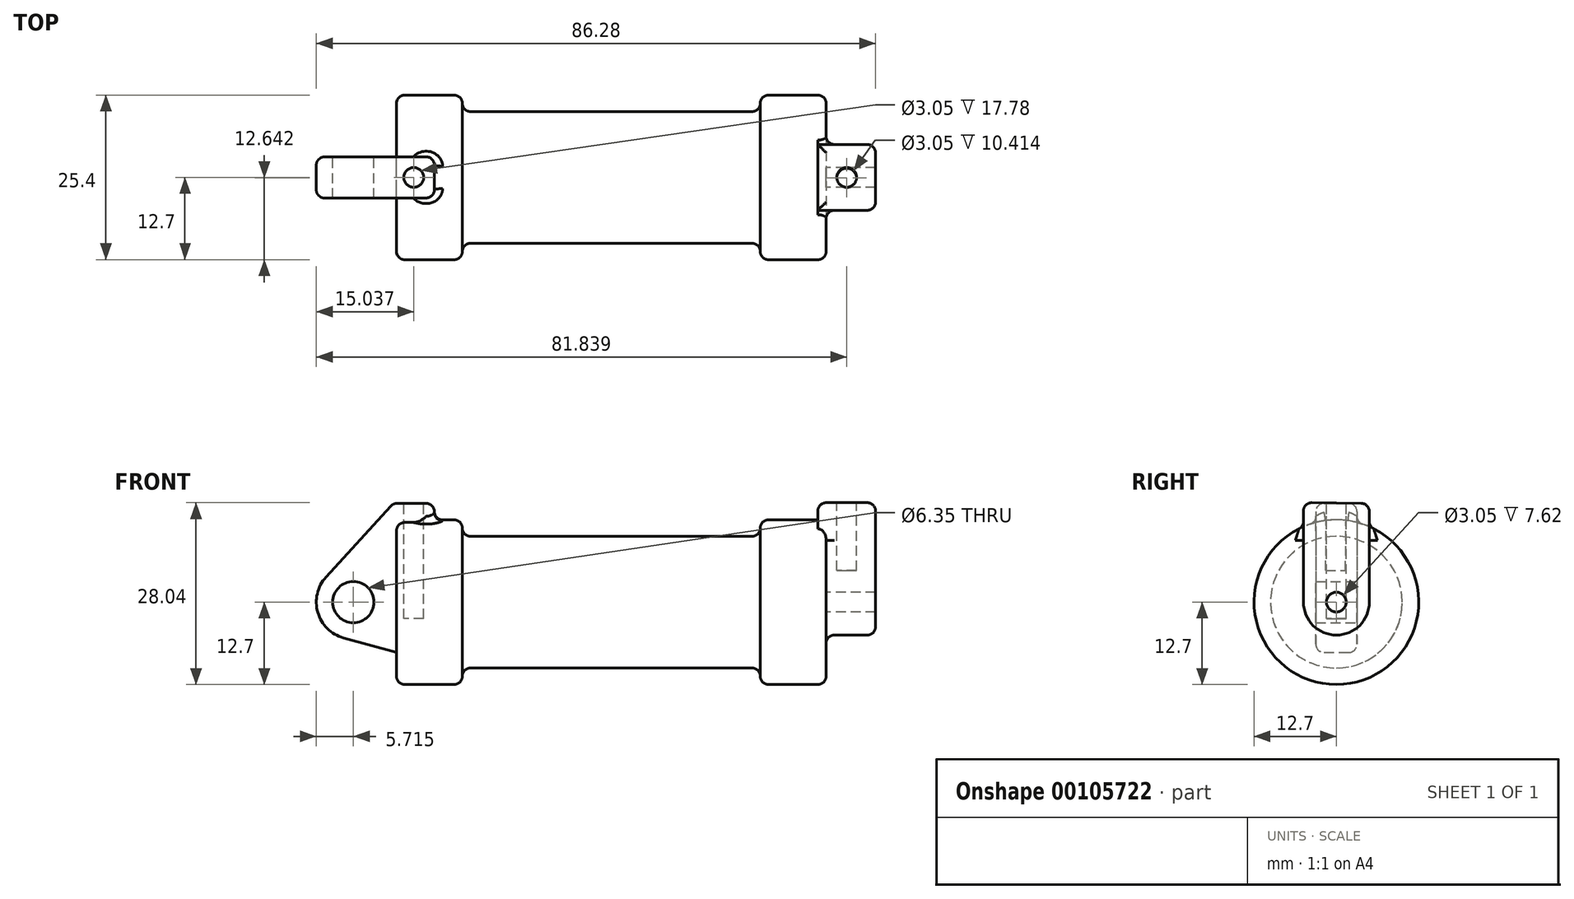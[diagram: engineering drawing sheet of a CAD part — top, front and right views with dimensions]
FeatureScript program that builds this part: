
annotation { "Feature Type Name" : "Feature", "Feature Type Description" : "" }
export const myFeature = defineFeature(function(context is Context, id is Id, definition is map)
    precondition{}
    {
        {
            var Q0;
            Q0=qCreatedBy(makeId("Front.planeOp"),FACE);
            var sketch = newSketch(context, id + "F0", { "sketchPlane" : qUnion([Q0])});
            skLineSegment(sketch, "E0", {"start": v(0, 0) * mm, "end": v(0, 12.7) * mm});
            skLineSegment(sketch, "E1", {"start": v(0, 12.7) * mm, "end": v(10.16, 12.7) * mm});
            skLineSegment(sketch, "E2", {"start": v(10.16, 12.7) * mm, "end": v(10.16, 10.16) * mm});
            skLineSegment(sketch, "E3", {"start": v(10.16, 10.16) * mm, "end": v(56.13, 10.16) * mm});
            skLineSegment(sketch, "E4", {"start": v(56.13, 10.16) * mm, "end": v(56.13, 12.7) * mm});
            skLineSegment(sketch, "E5", {"start": v(56.13, 12.7) * mm, "end": v(66.3, 12.7) * mm});
            skLineSegment(sketch, "E6", {"start": v(66.3, 12.7) * mm, "end": v(66.3, 0) * mm});
            skLineSegment(sketch, "E7", {"start": v(66.3, 0) * mm, "end": v(0, 0) * mm});
            skLineSegment(sketch, "E8", {"start": v(5.84, 15.24) * mm, "end": v(-0.5, 15.24) * mm});
            skLineSegment(sketch, "E9", {"start": v(-0.5, 15.24) * mm, "end": v(-10.88, 3.85) * mm});
            skLineSegment(sketch, "E10", {"start": v(0, 0) * mm, "end": v(-6.65, 0) * mm});
            skCircle(sketch, "E11", {"center": v(-6.65, 0) * mm, "radius": 5.72 * mm});
            skCircle(sketch, "E12", {"center": v(-6.65, 0) * mm, "radius": 3.18 * mm});
            skLineSegment(sketch, "E13", {"start": v(5.84, 15.24) * mm, "end": v(5.84, -9.4) * mm});
            skLineSegment(sketch, "E14", {"start": v(5.84, -9.4) * mm, "end": v(-8.18, -5.5) * mm});
            skSolve(sketch);
        }
        {
            var Q0;
            {var subQ0=sQuery(id+"F0.wireOp",EDGE,"E2");Q0=makeQuery(id+"F0.imprint","IMPRINT",FACE,{"disambiguationData":[TD([[makeQuery(id+"F0.imprint","IMPRINT",EDGE,{"derivedFrom":subQ0}),-1.0]])]});}
            var Q1;
            {var subQ0=sQuery(id+"F0.wireOp",EDGE,"E0");Q1=makeQuery(id+"F0.imprint","IMPRINT",FACE,{"disambiguationData":[TD([[makeQuery(id+"F0.imprint","IMPRINT",EDGE,{"derivedFrom":subQ0}),-1.0]])]});}
            var Q2;
            Q2=sQuery(id+"F0.wireOp",EDGE,"E7");
            revolve(context, id + "F1", {"entities" : qUnion([Q0, Q1]), "axis" : qUnion([Q2]), "revolveType" : RevolveType.FULL});
        }
        {
            var Q0;
            {var subQ3=sQuery(id+"F0.wireOp",EDGE,"E0");Q0=makeQuery(id+"F0.imprint","IMPRINT",FACE,{"disambiguationData":[TD([[makeQuery(id+"F0.imprint","IMPRINT",EDGE,{"derivedFrom":subQ3}),1.0]])]});}
            var Q1;
            {var subQ0=sQuery(id+"F0.wireOp",EDGE,"E14");Q1=makeQuery(id+"F0.imprint","IMPRINT",FACE,{"disambiguationData":[TD([[makeQuery(id+"F0.imprint","IMPRINT",EDGE,{"derivedFrom":subQ0}),-1.0]])]});}
            var Q2;
            {var subQ4=sQuery(id+"F0.wireOp",EDGE,"E12");Q2=makeQuery(id+"F0.imprint","IMPRINT",FACE,{"disambiguationData":[TD([[makeQuery(id+"F0.imprint","IMPRINT",EDGE,{"derivedFrom":subQ4}),-1.0]])]});}
            var Q3;
            {var subQ0=sQuery(id+"F0.wireOp",EDGE,"E0");Q3=makeQuery(id+"F0.imprint","IMPRINT",FACE,{"disambiguationData":[TD([[makeQuery(id+"F0.imprint","IMPRINT",EDGE,{"derivedFrom":subQ0}),-1.0]])]});}
            var Q4;
            Q4 = qSketchRegion(id + "F3", true);
            extrude(context, id + "F2", {"entities" : qUnion([Q0, Q1, Q2, Q3, Q4]), "operationType" : NewBodyOperationType.ADD, "endBound" : BoundingType.SYMMETRIC, "depth" : 6.35 * mm});
        }
        {
            var Q0;
            Q0=makeQuery(id+"F1.opRevolve","SWEPT_FACE",FACE,{"disambiguationData":[OSD([sQuery(id+"F0.wireOp",EDGE,"E6")])]});
            var sketch = newSketch(context, id + "F3", { "sketchPlane" : qUnion([Q0])});
            skCircle(sketch, "E15", {"center": v(0, 0) * mm, "radius": 1.52 * mm});
            skCircle(sketch, "E16", {"center": v(0, 0) * mm, "radius": 5.08 * mm});
            skLineSegment(sketch, "E17", {"start": v(-5.08, 0) * mm, "end": v(-5.08, 15.35) * mm});
            skLineSegment(sketch, "E18", {"start": v(5.08, 0) * mm, "end": v(5.08, 15.24) * mm});
            skLineSegment(sketch, "E19", {"start": v(-5.08, 15.35) * mm, "end": v(5.08, 15.24) * mm});
            skSolve(sketch);
        }
        {
            var Q0;
            Q0=makeQuery(id+"F3.imprint","IMPRINT",FACE,{"disambiguationData":[TD([[makeQuery(id+"F3.imprint","IMPRINT",EDGE,{"derivedFrom":sQuery(id+"F3.wireOp",EDGE,"E15")}),-1.0]])]});
            var Q1;
            {var subQ0=sQuery(id+"F3.wireOp",EDGE,"E17");var subQ1=sQuery(id+"F3.wireOp",EDGE,"E16");var subQ2=makeQuery(id+"F3.imprint","INTERSECT",VERTEX,{"derivedFrom":[subQ1,subQ0]});Q1=makeQuery(id+"F3.imprint","IMPRINT",FACE,{"disambiguationData":[TD([[makeQuery(id+"F3.imprint","IMPRINT",EDGE,{"disambiguationData":[TD([[subQ2,1.0]])],"derivedFrom":subQ1}),-1.0]])]});}
            var Q2;
            {var subQ0=sQuery(id+"F3.wireOp",EDGE,"E19");Q2=makeQuery(id+"F3.imprint","IMPRINT",FACE,{"disambiguationData":[TD([[makeQuery(id+"F3.imprint","IMPRINT",EDGE,{"derivedFrom":subQ0}),-1.0]])]});}
            extrude(context, id + "F4", {"entities" : qUnion([Q0, Q1, Q2]), "operationType" : NewBodyOperationType.ADD, "depth" : 7.62 * mm, "hasSecondDirection" : true, "secondDirectionOppositeDirection" : true, "secondDirectionDepth" : 1.27 * mm});
        }
        {
            var Q0;
            Q0=makeQuery(id+"F2.opExtrude","SWEPT_FACE",FACE,{"disambiguationData":[OSD([sQuery(id+"F0.wireOp",EDGE,"E8")])]});
            var sketch = newSketch(context, id + "F5", { "sketchPlane" : qUnion([Q0])});
            skPoint(sketch, "E20.centerSnap0", {"position": v(-0.5, 0) * mm});
            skLineSegment(sketch, "E21", {"start": v(-0.5, 0) * mm, "end": v(5.84, 0) * mm, "construction": true});
            skLineSegment(sketch, "E22", {"start": v(2.67, 3.18) * mm, "end": v(2.67, -3.18) * mm, "construction": true});
            skCircle(sketch, "E23", {"center": v(2.67, 0) * mm, "radius": 1.52 * mm});
            skSolve(sketch);
        }
        {
            var Q0;
            Q0=makeQuery(id+"F4.opExtrude","SWEPT_FACE",FACE,{"disambiguationData":[OSD([sQuery(id+"F3.wireOp",EDGE,"E19")])]});
            var sketch = newSketch(context, id + "F6", { "sketchPlane" : qUnion([Q0])});
            skLineSegment(sketch, "E24", {"start": v(69.47, 4.9) * mm, "end": v(69.47, -5.25) * mm, "construction": true});
            skLineSegment(sketch, "E25", {"start": v(65.02, -0.17) * mm, "end": v(73.91, -0.17) * mm, "construction": true});
            skCircle(sketch, "E26", {"center": v(69.47, -0.17) * mm, "radius": 1.52 * mm});
            skSolve(sketch);
        }
        {
            var Q0;
            Q0=makeQuery(id+"F5.imprint","IMPRINT",FACE,{"disambiguationData":[TD([[makeQuery(id+"F5.imprint","IMPRINT",EDGE,{"derivedFrom":sQuery(id+"F5.wireOp",EDGE,"E23")}),1.0]])]});
            extrude(context, id + "F7", {"entities" : qUnion([Q0]), "operationType" : NewBodyOperationType.REMOVE, "oppositeDirection" : true, "depth" : 17.78 * mm});
        }
        {
            var Q0;
            Q0=makeQuery(id+"F6.imprint","IMPRINT",FACE,{"disambiguationData":[TD([[makeQuery(id+"F6.imprint","IMPRINT",EDGE,{"derivedFrom":sQuery(id+"F6.wireOp",EDGE,"E26")}),1.0]])]});
            extrude(context, id + "F8", {"entities" : qUnion([Q0]), "operationType" : NewBodyOperationType.REMOVE, "oppositeDirection" : true, "depth" : 10.4 * mm});
        }
        {
            var Q0;
            Q0=makeQuery(id+"F1.opRevolve","SWEPT_EDGE",EDGE,{"disambiguationData":[OSD([sQuery(id+"F0.wireOp",EDGE,"E1"),sQuery(id+"F0.wireOp",EDGE,"E2")])]});
            var Q1;
            Q1=makeQuery(id+"F1.opRevolve","SWEPT_EDGE",EDGE,{"disambiguationData":[OSD([sQuery(id+"F0.wireOp",EDGE,"E2"),sQuery(id+"F0.wireOp",EDGE,"E3")])]});
            var Q2;
            Q2=makeQuery(id+"F1.opRevolve","SWEPT_EDGE",EDGE,{"disambiguationData":[OSD([sQuery(id+"F0.wireOp",EDGE,"E4"),sQuery(id+"F0.wireOp",EDGE,"E5")])]});
            var Q3;
            Q3=makeQuery(id+"F1.opRevolve","SWEPT_EDGE",EDGE,{"disambiguationData":[OSD([sQuery(id+"F0.wireOp",EDGE,"E5"),sQuery(id+"F0.wireOp",EDGE,"E6")])]});
            var Q4;
            Q4=makeQuery(id+"F1.opRevolve","SWEPT_EDGE",EDGE,{"disambiguationData":[OSD([sQuery(id+"F0.wireOp",EDGE,"E3"),sQuery(id+"F0.wireOp",EDGE,"E4")])]});
            var Q5;
            Q5=makeQuery(id+"F1.opRevolve","SWEPT_EDGE",EDGE,{"disambiguationData":[OSD([sQuery(id+"F0.wireOp",EDGE,"E0"),sQuery(id+"F0.wireOp",EDGE,"E1")])]});
            fillet(context, id + "F9", {"entities" : qUnion([Q0, Q1, Q2, Q3, Q4, Q5]), "radius" : 1.27 * mm, "tangentPropagation" : true, "allowEdgeOverflow" : false});
        }
        {
            var Q0;
            Q0=makeQuery(id+"F2.opExtrude","CAP_EDGE",EDGE,{"disambiguationData":[OSD([sQuery(id+"F0.wireOp",EDGE,"E9")])],"isStart":false});
            var Q1;
            Q1=makeQuery(id+"F2.opExtrude","CAP_EDGE",EDGE,{"disambiguationData":[OSD([sQuery(id+"F0.wireOp",EDGE,"E9")])],"isStart":true});
            var Q2;
            Q2=makeQuery(id+"F2.opExtrude","SWEPT_EDGE",EDGE,{"disambiguationData":[OSD([sQuery(id+"F0.wireOp",EDGE,"E9"),sQuery(id+"F0.wireOp",EDGE,"E11")])]});
            var Q3;
            Q3=makeQuery(id+"F2.opExtrude","SWEPT_EDGE",EDGE,{"disambiguationData":[OSD([sQuery(id+"F0.wireOp",EDGE,"E8"),sQuery(id+"F0.wireOp",EDGE,"E9")])]});
            var Q4;
            Q4=makeQuery(id+"F2.opExtrude","CAP_EDGE",EDGE,{"disambiguationData":[OSD([sQuery(id+"F0.wireOp",EDGE,"E8")])],"isStart":true});
            var Q5;
            Q5=makeQuery(id+"F2.opExtrude","CAP_EDGE",EDGE,{"disambiguationData":[OSD([sQuery(id+"F0.wireOp",EDGE,"E8")])],"isStart":false});
            var Q6;
            Q6=makeQuery(id+"F2.opExtrude","SWEPT_EDGE",EDGE,{"disambiguationData":[OSD([sQuery(id+"F0.wireOp",EDGE,"E8"),sQuery(id+"F0.wireOp",EDGE,"E13")])]});
            var Q7;
            Q7=makeQuery(id+"F2.opExtrude","CAP_EDGE",EDGE,{"disambiguationData":[OSD([sQuery(id+"F0.wireOp",EDGE,"E11")])],"isStart":false});
            var Q8;
            Q8=makeQuery(id+"F2.opExtrude","CAP_EDGE",EDGE,{"disambiguationData":[OSD([sQuery(id+"F0.wireOp",EDGE,"E14")])],"isStart":false});
            var Q9;
            Q9=makeQuery(id+"F2.opExtrude","CAP_EDGE",EDGE,{"disambiguationData":[OSD([sQuery(id+"F0.wireOp",EDGE,"E13")])],"isStart":false});
            var Q10;
            Q10=makeQuery(id+"F2.opExtrude","CAP_EDGE",EDGE,{"disambiguationData":[OSD([sQuery(id+"F0.wireOp",EDGE,"E13")])],"isStart":true});
            var Q11;
            Q11=makeQuery(id+"F2.boolean.opBoolean","INTERSECT",EDGE,{"derivedFrom":[makeQuery(id+"F1.opRevolve","SWEPT_FACE",FACE,{"disambiguationData":[OSD([sQuery(id+"F0.wireOp",EDGE,"E1")])]}),makeQuery(id+"F2.opExtrude","SWEPT_FACE",FACE,{"disambiguationData":[OSD([sQuery(id+"F0.wireOp",EDGE,"E13")])]})]});
            fillet(context, id + "F10", {"entities" : qUnion([Q0, Q1, Q2, Q3, Q4, Q5, Q6, Q7, Q8, Q9, Q10, Q11]), "radius" : 1.27 * mm, "tangentPropagation" : true, "allowEdgeOverflow" : false});
        }
        {
            var Q0;
            Q0=makeQuery(id+"F4.opExtrude","SWEPT_EDGE",EDGE,{"disambiguationData":[OSD([sQuery(id+"F3.wireOp",EDGE,"E17"),sQuery(id+"F3.wireOp",EDGE,"E19")])]});
            var Q1;
            Q1=makeQuery(id+"F4.opExtrude","CAP_EDGE",EDGE,{"disambiguationData":[OSD([sQuery(id+"F3.wireOp",EDGE,"E19")])],"isStart":false});
            var Q2;
            Q2=makeQuery(id+"F4.opExtrude","SWEPT_EDGE",EDGE,{"disambiguationData":[OSD([sQuery(id+"F3.wireOp",EDGE,"E18"),sQuery(id+"F3.wireOp",EDGE,"E19")])]});
            var Q3;
            Q3=makeQuery(id+"F4.opExtrude","CAP_EDGE",EDGE,{"disambiguationData":[OSD([sQuery(id+"F3.wireOp",EDGE,"E17")])],"isStart":false});
            var Q4;
            Q4=makeQuery(id+"F4.opExtrude","CAP_EDGE",EDGE,{"disambiguationData":[OSD([sQuery(id+"F3.wireOp",EDGE,"E18")])],"isStart":false});
            var Q5;
            Q5=makeQuery(id+"F4.opExtrude","CAP_EDGE",EDGE,{"disambiguationData":[OSD([sQuery(id+"F3.wireOp",EDGE,"E16")])],"isStart":false});
            var Q6;
            Q6=makeQuery(id+"F4.boolean.opBoolean","INTERSECT",EDGE,{"derivedFrom":[makeQuery(id+"F1.opRevolve","SWEPT_FACE",FACE,{"disambiguationData":[OSD([sQuery(id+"F0.wireOp",EDGE,"E6")])]}),makeQuery(id+"F4.opExtrude","SWEPT_FACE",FACE,{"disambiguationData":[OSD([sQuery(id+"F3.wireOp",EDGE,"E17")])]})]});
            var Q7;
            Q7=makeQuery(id+"F4.boolean.opBoolean","INTERSECT",EDGE,{"derivedFrom":[makeQuery(id+"F1.opRevolve","SWEPT_FACE",FACE,{"disambiguationData":[OSD([sQuery(id+"F0.wireOp",EDGE,"E6")])]}),makeQuery(id+"F4.opExtrude","SWEPT_FACE",FACE,{"disambiguationData":[OSD([sQuery(id+"F3.wireOp",EDGE,"E16")])]})]});
            var Q8;
            Q8=makeQuery(id+"F9.opFillet","BLEND_EDGE",EDGE,{"blendedFrom":[makeQuery(id+"F1.opRevolve","SWEPT_EDGE",EDGE,{"disambiguationData":[OSD([sQuery(id+"F0.wireOp",EDGE,"E5"),sQuery(id+"F0.wireOp",EDGE,"E6")])]}),makeQuery(id+"F4.opExtrude","SWEPT_FACE",FACE,{"disambiguationData":[OSD([sQuery(id+"F3.wireOp",EDGE,"E17")])]})],"blendedInto":[makeQuery(id+"F4.opExtrude","SWEPT_FACE",FACE,{"disambiguationData":[OSD([sQuery(id+"F3.wireOp",EDGE,"E17")])]})]});
            var Q9;
            Q9=makeQuery(id+"F4.opExtrude","CAP_EDGE",EDGE,{"disambiguationData":[OSD([sQuery(id+"F3.wireOp",EDGE,"E19")])],"isStart":true});
            fillet(context, id + "F11", {"entities" : qUnion([Q0, Q1, Q2, Q3, Q4, Q5, Q6, Q7, Q8, Q9]), "radius" : 1.27 * mm, "tangentPropagation" : true, "allowEdgeOverflow" : false});
        }
    });
